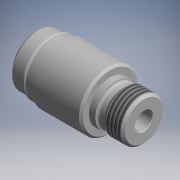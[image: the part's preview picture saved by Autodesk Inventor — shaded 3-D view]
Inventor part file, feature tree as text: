
AUTODESK INVENTOR PART (.ipt)
format: ipt  version: 2017.3 (Build 213256000, 256)  size: 261,632 bytes
history: native  units: mm (DEFAULTED — no unit token found)
features: other x119, sketch x6, revolve x5, thread x2, hole x1
ambient origin geometry x8: Origin, YZ Plane, XZ Plane, XY Plane, X Axis, Y Axis, Z Axis, Center Point
bodies: Solid1 (feature_tree)
feature tree (133):
  revolve  "Revolution1"  [1 undecoded]
  thread  "Thread1"  [1 undecoded]
  revolve  "Revolution2"  Angle=360.0deg
  hole  "Hole1"  [1 undecoded]
  revolve  "Revolution3"  [1 undecoded]
  revolve  "Revolution4"  [1 undecoded]
  thread  "Thread2"  [1 undecoded]
  revolve  "Revolution5"  [1 undecoded]
  other  "dp1_XY"
  other  "dp1_YZ"
  other  "dp1_ZX"
  other  "dp1_X"
  other  "dp1_Y"
  other  "dp1_Z"
  other  "dp1_Center"
  other  "dp2_XY"
  other  "dp2_YZ"
  other  "dp2_ZX"
  other  "dp2_X"
  other  "dp2_Y"
  other  "dp2_Z"
  other  "dp2_Center"
  other  "hh_XY"
  other  "hh_YZ"
  other  "hh_ZX"
  other  "hh_X"
  other  "hh_Y"
  other  "hh_Z"
  other  "hh_Center"
  other  "port_XY"
  other  "port_YZ"
  other  "port_ZX"
  other  "port_X"
  other  "port_Y"
  other  "port_Z"
  other  "port_Center"
  other  "rod_guide_XY"
  other  "rod_guide_YZ"
  other  "rod_guide_ZX"
  other  "rod_guide_X"
  other  "rod_guide_Y"
  other  "rod_guide_Z"
  other  "rod_guide_Center"
  other  "s1_XY"
  other  "s1_YZ"
  other  "s1_ZX"
  other  "s1_X"
  other  "s1_Y"
  other  "s1_Z"
  other  "s1_Center"
  other  "s2_XY"
  other  "s2_YZ"
  other  "s2_ZX"
  other  "s2_X"
  other  "s2_Y"
  other  "s2_Z"
  other  "s2_Center"
  other  "t1_XY"
  other  "t1_YZ"
  other  "t1_ZX"
  other  "t1_X"
  other  "t1_Y"
  other  "t1_Z"
  other  "t1_Center"
  other  "t111_XY"
  other  "t111_YZ"
  other  "t111_ZX"
  other  "t111_X"
  other  "t111_Y"
  other  "t111_Z"
  other  "t111_Center"
  other  "to_foot_bracket_XY"
  other  "to_foot_bracket_YZ"
  other  "to_foot_bracket_ZX"
  other  "to_foot_bracket_X"
  other  "to_foot_bracket_Y"
  other  "to_foot_bracket_Z"
  other  "to_foot_bracket_Center"
  other  "to_nut_XY"
  other  "to_nut_YZ"
  other  "to_nut_ZX"
  other  "to_nut_X"
  other  "to_nut_Y"
  other  "to_nut_Z"
  other  "to_nut_Center"
  other  "to_rod_XY"
  other  "to_rod_YZ"
  other  "to_rod_ZX"
  other  "to_rod_X"
  other  "to_rod_Y"
  other  "to_rod_Z"
  other  "to_rod_Center"
  other  "to_screw_XY"
  other  "to_screw_YZ"
  other  "to_screw_ZX"
  other  "to_screw_X"
  other  "to_screw_Y"
  other  "to_screw_Z"
  other  "to_screw_Center"
  other  "to_trunnion_brackets_XY"
  other  "to_trunnion_brackets_YZ"
  other  "to_trunnion_brackets_ZX"
  other  "to_trunnion_brackets_X"
  other  "to_trunnion_brackets_Y"
  other  "to_trunnion_brackets_Z"
  other  "to_trunnion_brackets_Center"
  other  "to_trunnion_brackets1_XY"
  other  "to_trunnion_brackets1_YZ"
  other  "to_trunnion_brackets1_ZX"
  other  "to_trunnion_brackets1_X"
  other  "to_trunnion_brackets1_Y"
  other  "to_trunnion_brackets1_Z"
  other  "to_trunnion_brackets1_Center"
  other  "to_trunnion_brackets2_XY"
  other  "to_trunnion_brackets2_YZ"
  other  "to_trunnion_brackets2_ZX"
  other  "to_trunnion_brackets2_X"
  other  "to_trunnion_brackets2_Y"
  other  "to_trunnion_brackets2_Z"
  other  "to_trunnion_brackets2_Center"
  other  "to_tube_XY"
  other  "to_tube_YZ"
  other  "to_tube_ZX"
  other  "to_tube_X"
  other  "to_tube_Y"
  other  "to_tube_Z"
  other  "to_tube_Center"
  sketch  "Sketch_2"  dims[d0=360.0deg d1=5.84212mm d2=0.0mm d3=360.0deg]
  sketch  "Sketch_3"  dims[d4=6.4389mm d5=6.0mm d6=6.9469mm d7=2.0mm d8=90.0deg d9=40.4876mm d10=0.0mm d11=360.0deg]
  sketch  "Sketch3"  dims[d12=360.0deg d13=3.17653mm d14=0.0mm]
  sketch  "Sketch_10"  dims[d15=360.0deg]
  sketch  "Sketch_43"  dims[d16=0.0mm d17=0.0mm d18=0.0mm d19=0.0mm d20=0.0mm]
  sketch  "Sketch_47"
note: 7 required parameter values undecoded (feature->parameter linkage not recoverable at this tier; creation-order binding heuristic only, values carry confidence <= 0.55)